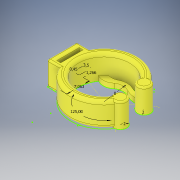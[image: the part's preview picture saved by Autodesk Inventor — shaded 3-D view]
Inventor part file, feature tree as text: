
AUTODESK INVENTOR PART (.ipt)
format: ipt  version: 2019 (Build 230136000, 136)  size: 670,208 bytes
history: native  units: mm
features: fillet x13, extrude x3, sketch x1
ambient origin geometry x8: Origin, YZ Plane, XZ Plane, XY Plane, X Axis, Y Axis, Z Axis, Center Point
bodies: Body1 (feature_tree)
feature tree (17):
  sketch  "Sketch1"  dims[d39=21.816616mm d40=8.0mm d113=10.0mm d114=2.0mm d115=2.0mm d118=0.07854mm d119=7.5mm d120=0.0mm d121=1.5mm d122=0.0mm d123=1.5mm d124=0.0mm d125=1.0mm d126=1.0mm d127=1.0mm d128=0.5mm d129=0.5mm d130=0.5mm d131=0.5mm d132=0.5mm d133=1.0mm d134=1.0mm d135=0.5mm d136=3.5mm d137=7.06251mm d138=1.266mm d141=0.5mm d142=0.5mm]
  extrude  "Extrusion8"  Depth=0.5mm
  extrude  "Extrusion9"  Depth=10.0mm
  extrude  "Extrusion10"  Depth=0.5mm
  fillet  "Fillet32"  Radius=2.0mm
  fillet  "Fillet33"  Radius=0.07854mm
  fillet  "Fillet34"  Radius=7.5mm
  fillet  "Fillet35"  Radius=1.5mm
  fillet  "Fillet36"  Radius=1.5mm
  fillet  "Fillet37"  Radius=1.0mm
  fillet  "Fillet38"  Radius=1.0mm
  fillet  "Fillet39"  Radius=1.0mm
  fillet  "Fillet40"  Radius=0.5mm
  fillet  "Fillet41"  Radius=0.5mm
  fillet  "Fillet42"  Radius=0.5mm
  fillet  "Fillet43"  Radius=0.5mm
  fillet  "Fillet44"  Radius=0.5mm
